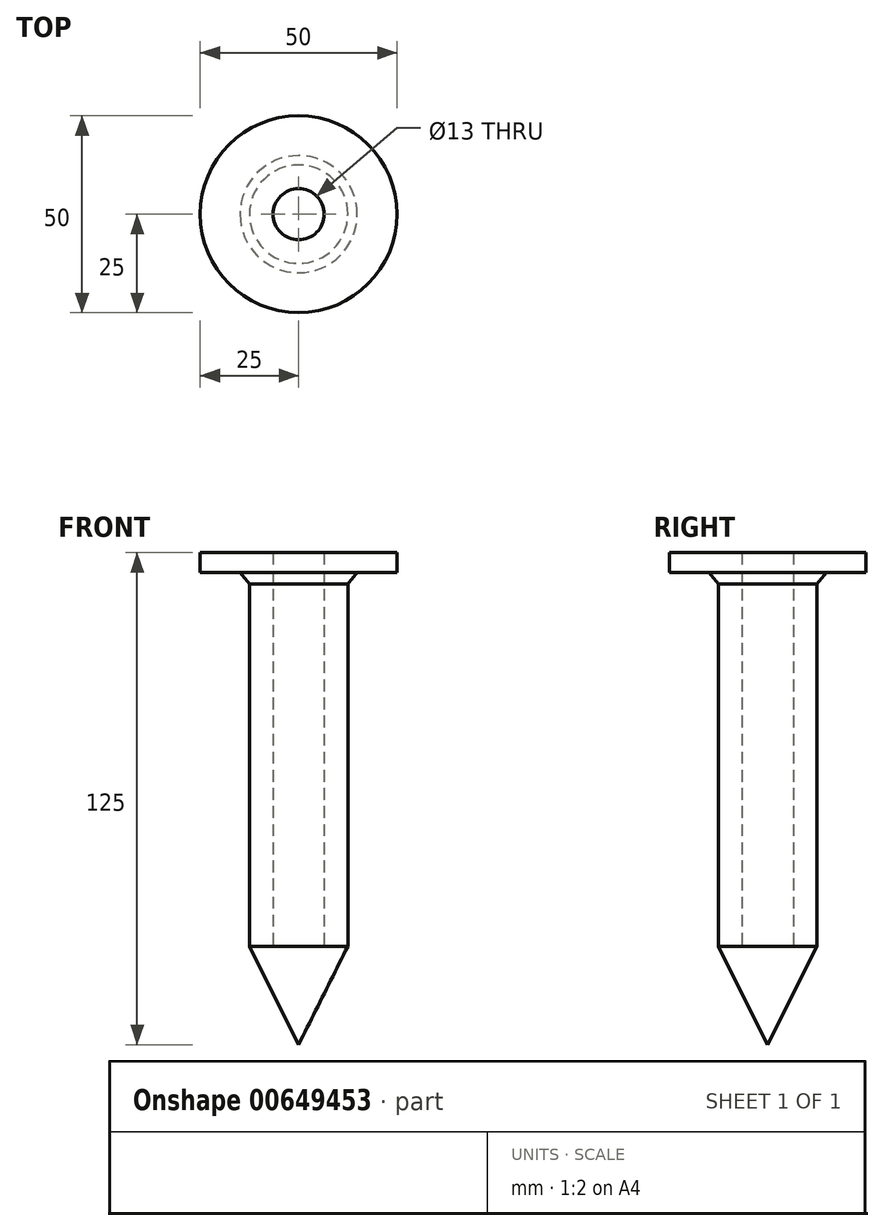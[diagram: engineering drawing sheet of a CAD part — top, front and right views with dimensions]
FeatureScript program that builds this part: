
annotation { "Feature Type Name" : "Feature", "Feature Type Description" : "" }
export const myFeature = defineFeature(function(context is Context, id is Id, definition is map)
    precondition{}
    {
        {
            var Q0;
            Q0=qCreatedBy(makeId("Top.planeOp"),FACE);
            var sketch = newSketch(context, id + "F0", { "sketchPlane" : qUnion([Q0])});
            skCircle(sketch, "E0", {"center": v(0, 0) * mm, "radius": 6.5 * mm});
            skCircle(sketch, "E1", {"center": v(0, 0) * mm, "radius": 12.5 * mm});
            skSolve(sketch);
        }
        {
            var Q0;
            Q0=makeQuery(id+"F0.imprint","IMPRINT",FACE,{"disambiguationData":[TD([[makeQuery(id+"F0.imprint","IMPRINT",EDGE,{"derivedFrom":sQuery(id+"F0.wireOp",EDGE,"E0")}),-1.0]])]});
            extrude(context, id + "F1", {"entities" : qUnion([Q0]), "depth" : 100 * mm, "offsetDistance" : 25 * mm});
        }
        {
            var Q0;
            Q0=qCreatedBy(makeId("Front.planeOp"),FACE);
            var sketch = newSketch(context, id + "F2", { "sketchPlane" : qUnion([Q0])});
            skLineSegment(sketch, "E2", {"start": v(0, 0) * mm, "end": v(0, -25) * mm});
            skLineSegment(sketch, "E3", {"start": v(0, 0) * mm, "end": v(12.5, 0) * mm});
            skLineSegment(sketch, "E4", {"start": v(12.5, 0) * mm, "end": v(0, -25) * mm});
            skSolve(sketch);
        }
        {
            var Q0;
            Q0=makeQuery(id+"F2.imprint","IMPRINT",FACE,{"disambiguationData":[TD([[makeQuery(id+"F2.imprint","IMPRINT",EDGE,{"derivedFrom":sQuery(id+"F2.wireOp",EDGE,"E2")}),1.0]])]});
            var Q1;
            Q1=sQuery(id+"F2.wireOp",EDGE,"E2");
            revolve(context, id + "F3", {"entities" : qUnion([Q0]), "axis" : qUnion([Q1]), "revolveType" : RevolveType.FULL});
        }
        {
            var Q0;
            Q0=qCreatedBy(makeId("Front.planeOp"),FACE);
            var sketch = newSketch(context, id + "F4", { "sketchPlane" : qUnion([Q0])});
            skLineSegment(sketch, "E5", {"start": v(0, 0) * mm, "end": v(0, 100) * mm});
            skLineSegment(sketch, "E6", {"start": v(0, 100) * mm, "end": v(25, 100) * mm});
            skLineSegment(sketch, "E7", {"start": v(25, 100) * mm, "end": v(25, 95) * mm});
            skLineSegment(sketch, "E8", {"start": v(25, 95) * mm, "end": v(10, 95) * mm});
            skLineSegment(sketch, "E9", {"start": v(10, 95) * mm, "end": v(10, 100) * mm});
            skPoint(sketch, "E9.endSnap0", {"position": v(12.5, 100) * mm});
            skLineSegment(sketch, "E10", {"start": v(14.89, 95) * mm, "end": v(10, 89.01) * mm});
            skLineSegment(sketch, "E11", {"start": v(10, 89.01) * mm, "end": v(10, 95) * mm});
            skSolve(sketch);
        }
        {
            var Q0;
            {var subQ2=sQuery(id+"F4.wireOp",EDGE,"E10");Q0=makeQuery(id+"F4.imprint","IMPRINT",FACE,{"disambiguationData":[TD([[makeQuery(id+"F4.imprint","IMPRINT",EDGE,{"derivedFrom":subQ2}),-1.0]])]});}
            var Q1;
            {var subQ3=sQuery(id+"F4.wireOp",EDGE,"E7");Q1=makeQuery(id+"F4.imprint","IMPRINT",FACE,{"disambiguationData":[TD([[makeQuery(id+"F4.imprint","IMPRINT",EDGE,{"derivedFrom":subQ3}),-1.0]])]});}
            var Q2;
            Q2=sQuery(id+"F4.wireOp",EDGE,"E5");
            revolve(context, id + "F5", {"operationType" : NewBodyOperationType.ADD, "entities" : qUnion([Q0, Q1]), "axis" : qUnion([Q2]), "revolveType" : RevolveType.FULL});
        }
    });
